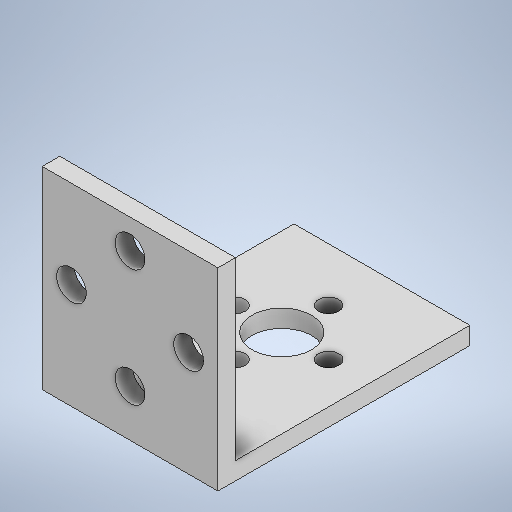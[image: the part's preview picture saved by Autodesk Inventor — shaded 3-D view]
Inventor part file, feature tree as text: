
AUTODESK INVENTOR PART (.ipt)
format: ipt  version: 2025.2 (Build 292293000, 293)  size: 273,920 bytes
history: native  units: mm
features: sketch x3, extrude x3
ambient origin geometry x8: Origin, YZ Plane, XZ Plane, XY Plane, X Axis, Y Axis, Z Axis, Center Point
bodies: Solid1 (feature_tree)
feature tree (6):
  sketch  "Sketch1"  dims[d0=30.0mm d1=30.0mm]
  extrude  "Extrusion1"  Depth=30.0mm
  extrude  "Extrusion2"  Depth=20.0mm
  extrude  "Extrusion3"  Depth=5.1mm
  sketch  "Sketch2"  dims[d4=5.1mm d5=5.1mm d6=5.1mm d7=5.1mm d8=3.0mm d9=3.0mm d10=0.0mm d11=40.0mm d12=0.0mm d13=22.896mm d14=10.2mm d15=16.0mm d16=3.5mm d17=40.0mm d19=360.0deg d21=40.0mm d22=0.0mm]
  sketch  "Sketch Circular Pattern1"  dims[d2=20.0mm d3=20.0mm]
